# Revit family: Legrand Coffrets HYPRA non percés avec ou sans rail
name_source: partatom
category: Equipement électrique
units: mm (PartAtom-declared; Revit-internal decimal feet)

## family parameters
Basée sur le plan de construction = Non
Configuration du panneau = Deux colonnes, circuits au sein
Cote de connecteur circulaire = Utiliser le diamètre
Couper avec des vides une fois chargée = Non
Numéro OmniClass = 23.80.30.11.17
Partagée = Non
Point de calcul de pièce = Non
Titre OmniClass = Distribution Boards and Control Panels
Toujours verticalement = Oui
Type d'élément = Tableau de raccordement

## types (6) — shared parameters
Classe de protection = Max IP66
Conditions Générale d'Utilisation = https://export.legrand.com
Description = Coffrets HYPRA non percé
Fabricant = Legrand
URL = www.legrand.fr
zero-valued in all types: Elévation par défaut

## per-type parameters (varying)
| type | Nombre de prises | Rail modulaire | Référence 059841 | Référence 059842 | Référence 059843 | Référence 059844 | Référence 059845 | Référence 059849 |
| Référence 059841 | 2x16A ou 32A | Aucun | Oui | Non | Non | Non | Non | Non |
| Référence 059842 | 6x16A ou 32A | Aucun | Non | Oui | Non | Non | Non | Non |
| Référence 059843 | 2x16A ou 32A | 6 modules | Non | Non | Oui | Non | Non | Non |
| Référence 059844 | 4x16A ou 32A | 9 modules | Non | Non | Non | Oui | Non | Non |
| Référence 059845 | 6x16A ou 32A | 2x9 modules | Non | Non | Non | Non | Oui | Non |
| Référence 059849 | Aucun | 2x9 modules | Non | Non | Non | Non | Non | Oui |

note: column(s) folded — value = type name in every type: Modèle
